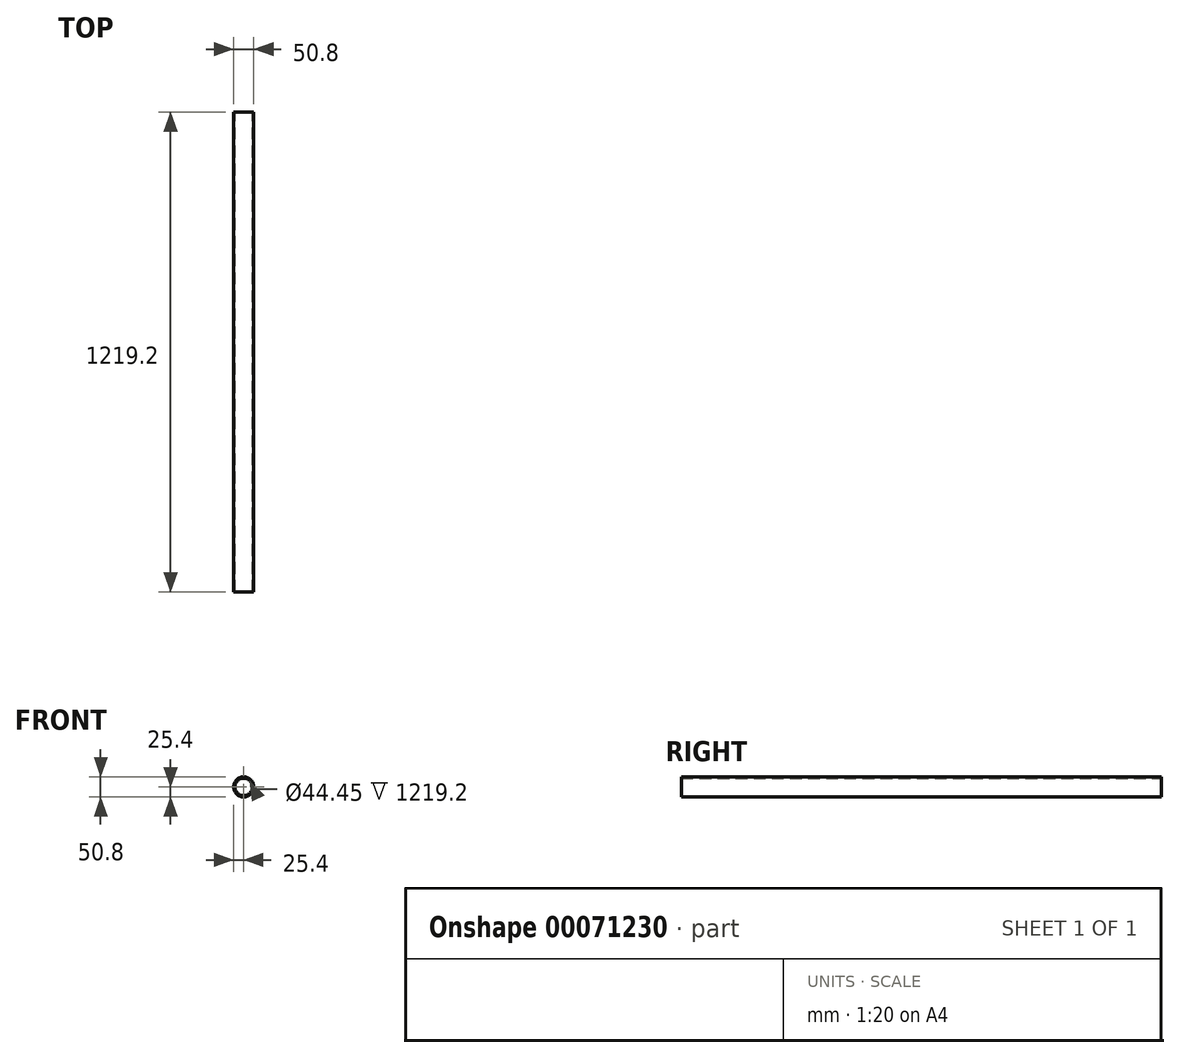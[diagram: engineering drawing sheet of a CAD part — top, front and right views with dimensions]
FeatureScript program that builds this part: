
annotation { "Feature Type Name" : "Feature", "Feature Type Description" : "" }
export const myFeature = defineFeature(function(context is Context, id is Id, definition is map)
    precondition{}
    {
        {
            var Q0;
            Q0=qCreatedBy(makeId("Front.planeOp"),FACE);
            var sketch = newSketch(context, id + "F0", { "sketchPlane" : qUnion([Q0])});
            skCircle(sketch, "E0", {"center": v(0, 0) * mm, "radius": 25.4 * mm});
            skCircle(sketch, "E1", {"center": v(0, 0) * mm, "radius": 22.23 * mm});
            skSolve(sketch);
        }
        {
            var Q0;
            Q0=makeQuery(id+"F0.imprint","IMPRINT",FACE,{"disambiguationData":[TD([[makeQuery(id+"F0.imprint","IMPRINT",EDGE,{"derivedFrom":sQuery(id+"F0.wireOp",EDGE,"E0")}),1.0]])]});
            extrude(context, id + "F1", {"entities" : qUnion([Q0]), "depth" : 1219.2 * mm});
        }
    });
